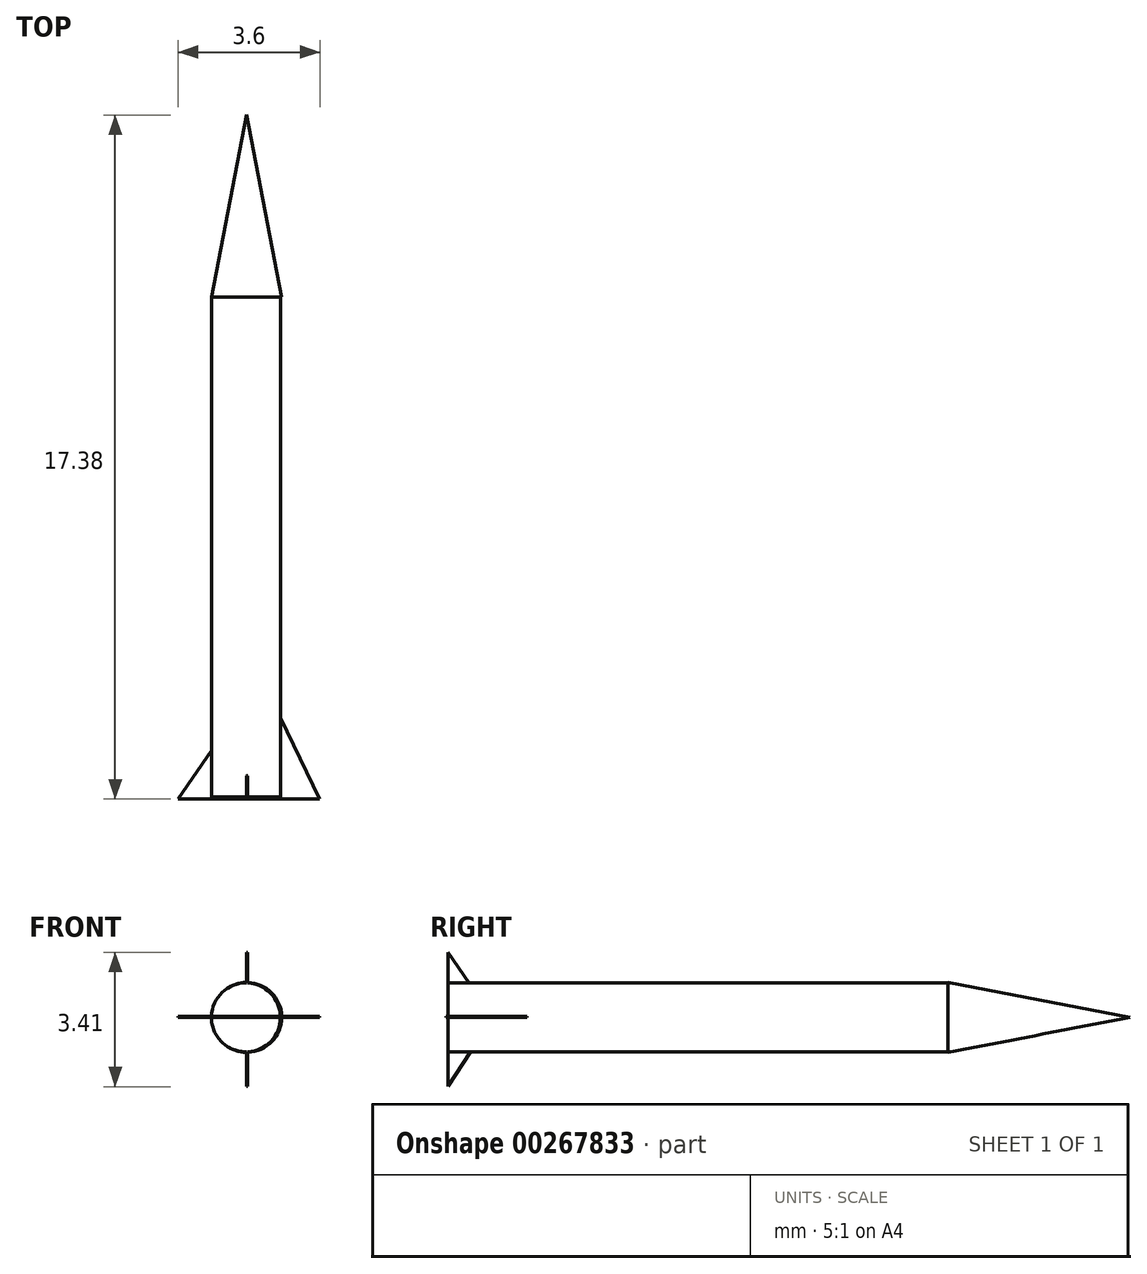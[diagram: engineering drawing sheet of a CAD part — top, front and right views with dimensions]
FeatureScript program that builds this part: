
annotation { "Feature Type Name" : "Feature", "Feature Type Description" : "" }
export const myFeature = defineFeature(function(context is Context, id is Id, definition is map)
    precondition{}
    {
        {
            var Q0;
            Q0=qCreatedBy(makeId("Front.planeOp"),FACE);
            var sketch = newSketch(context, id + "F0", { "sketchPlane" : qUnion([Q0])});
            skCircle(sketch, "E0", {"center": v(-0.02, 0) * mm, "radius": 0.88 * mm});
            skSolve(sketch);
        }
        {
            var Q0;
            Q0 = qSketchRegion(id + "F0", true);
            extrude(context, id + "F1", {"entities" : qUnion([Q0]), "depth" : 12.7 * mm});
        }
        {
            var Q0;
            Q0=qCreatedBy(makeId("Right.planeOp"),FACE);
            var sketch = newSketch(context, id + "F2", { "sketchPlane" : qUnion([Q0])});
            skLineSegment(sketch, "E1", {"start": v(0, 0) * mm, "end": v(4.63, 0) * mm});
            skLineSegment(sketch, "E2", {"start": v(4.63, 0) * mm, "end": v(0, 0.89) * mm});
            skLineSegment(sketch, "E3", {"start": v(0, 0.89) * mm, "end": v(0, 0) * mm});
            skSolve(sketch);
        }
        {
            var Q0;
            Q0 = qSketchRegion(id + "F2", true);
            var Q1;
            Q1=sQuery(id+"F2.wireOp",EDGE,"E1");
            revolve(context, id + "F3", {"operationType" : NewBodyOperationType.ADD, "entities" : qUnion([Q0]), "axis" : qUnion([Q1]), "revolveType" : RevolveType.FULL});
        }
        {
            var Q0;
            Q0=qCreatedBy(makeId("Top.planeOp"),FACE);
            var sketch = newSketch(context, id + "F4", { "sketchPlane" : qUnion([Q0])});
            skLineSegment(sketch, "E4", {"start": v(-1.74, -12.75) * mm, "end": v(1.86, -12.75) * mm});
            skLineSegment(sketch, "E5", {"start": v(1.86, -12.75) * mm, "end": v(0.36, -9.67) * mm});
            skLineSegment(sketch, "E6", {"start": v(0.36, -9.67) * mm, "end": v(-1.74, -12.75) * mm});
            skSolve(sketch);
        }
        {
            var Q0;
            Q0 = qSketchRegion(id + "F4", true);
            extrude(context, id + "F5", {"entities" : qUnion([Q0]), "operationType" : NewBodyOperationType.ADD, "depth" : 0.03 * mm});
        }
        {
            var Q0;
            Q0=qCreatedBy(makeId("Right.planeOp"),FACE);
            var sketch = newSketch(context, id + "F6", { "sketchPlane" : qUnion([Q0])});
            skLineSegment(sketch, "E7", {"start": v(-12.7, 1.65) * mm, "end": v(-12.7, -1.76) * mm});
            skLineSegment(sketch, "E8", {"start": v(-12.7, -1.76) * mm, "end": v(-11.56, 0) * mm});
            skLineSegment(sketch, "E9", {"start": v(-11.56, 0) * mm, "end": v(-12.7, 1.65) * mm});
            skSolve(sketch);
        }
        {
            var Q0;
            Q0 = qSketchRegion(id + "F6", true);
            extrude(context, id + "F7", {"entities" : qUnion([Q0]), "operationType" : NewBodyOperationType.ADD, "depth" : 0.03 * mm});
        }
    });
